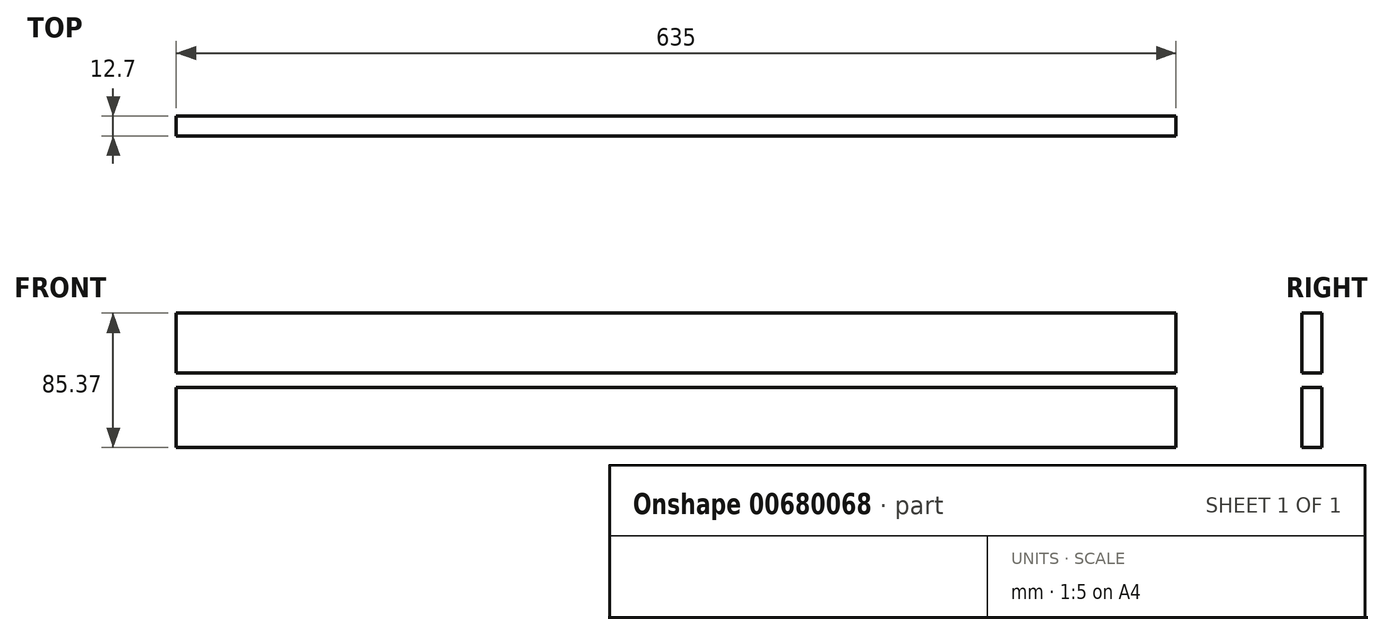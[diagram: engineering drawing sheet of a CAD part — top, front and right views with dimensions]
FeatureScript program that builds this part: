
annotation { "Feature Type Name" : "Feature", "Feature Type Description" : "" }
export const myFeature = defineFeature(function(context is Context, id is Id, definition is map)
    precondition{}
    {
        {
            var Q0;
            Q0=qCreatedBy(makeId("Front.planeOp"),FACE);
            var sketch = newSketch(context, id + "F0", { "sketchPlane" : qUnion([Q0])});
            skLineSegment(sketch, "E0.bottom", {"start": v(-317.5, 19.05) * mm, "end": v(317.5, 19.05) * mm});
            skLineSegment(sketch, "E0.top", {"start": v(-317.5, -19.05) * mm, "end": v(317.5, -19.05) * mm});
            skLineSegment(sketch, "E0.left", {"start": v(-317.5, 19.05) * mm, "end": v(-317.5, -19.05) * mm});
            skLineSegment(sketch, "E0.right", {"start": v(317.5, 19.05) * mm, "end": v(317.5, -19.05) * mm});
            skPoint(sketch, "E0.middle", {"position": v(0, 0) * mm});
            skLineSegment(sketch, "E1.bottom", {"start": v(-317.5, 66.32) * mm, "end": v(317.5, 66.32) * mm});
            skLineSegment(sketch, "E1.top", {"start": v(-317.5, 28.22) * mm, "end": v(317.5, 28.22) * mm});
            skLineSegment(sketch, "E1.left", {"start": v(-317.5, 66.32) * mm, "end": v(-317.5, 28.22) * mm});
            skLineSegment(sketch, "E1.right", {"start": v(317.5, 66.32) * mm, "end": v(317.5, 28.22) * mm});
            skPoint(sketch, "E1.middle", {"position": v(0, 47.27) * mm});
            skSolve(sketch);
        }
        {
            var Q0;
            Q0=makeQuery(id+"F0.imprint","IMPRINT",FACE,{"disambiguationData":[TD([[makeQuery(id+"F0.imprint","IMPRINT",EDGE,{"derivedFrom":sQuery(id+"F0.wireOp",EDGE,"E1.bottom")}),-1.0]])]});
            var Q1;
            Q1=makeQuery(id+"F0.imprint","IMPRINT",FACE,{"disambiguationData":[TD([[makeQuery(id+"F0.imprint","IMPRINT",EDGE,{"derivedFrom":sQuery(id+"F0.wireOp",EDGE,"E0.bottom")}),-1.0]])]});
            extrude(context, id + "F1", {"entities" : qUnion([Q0, Q1]), "depth" : 12.7 * mm, "offsetDistance" : 25.4 * mm});
        }
    });
